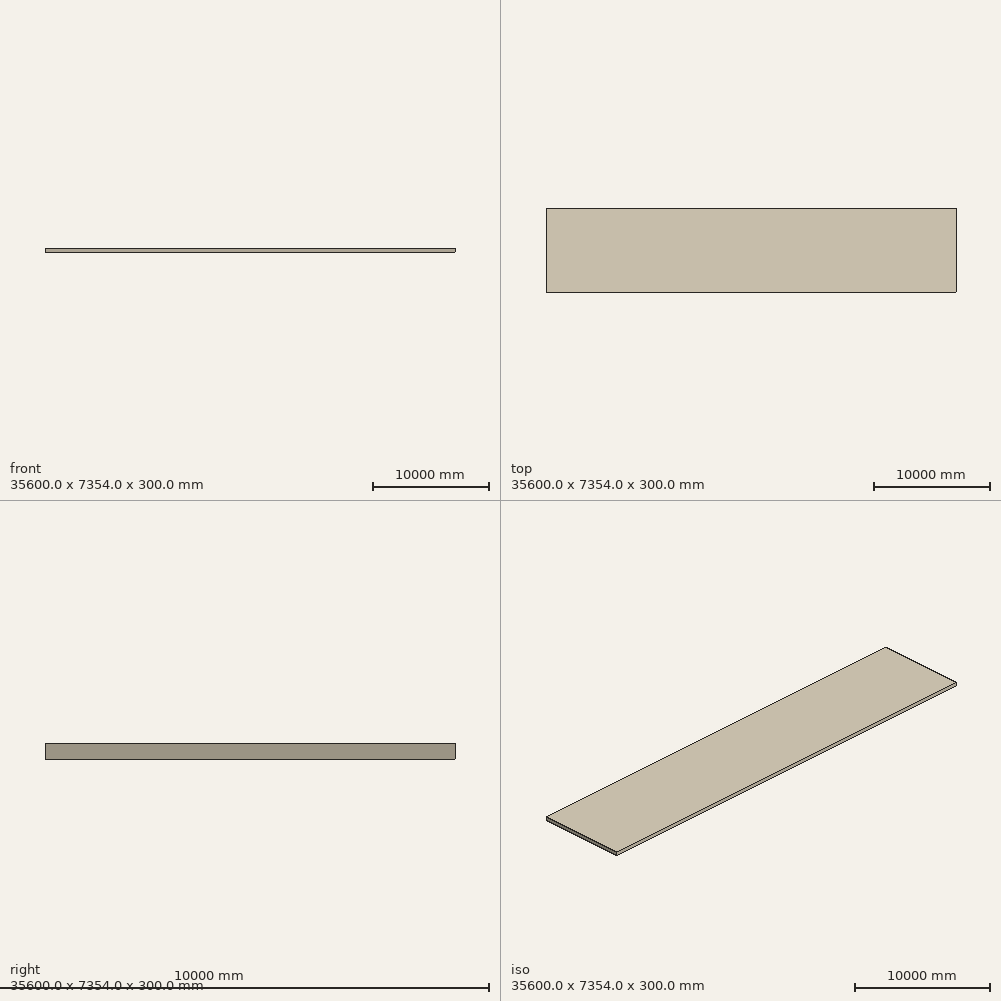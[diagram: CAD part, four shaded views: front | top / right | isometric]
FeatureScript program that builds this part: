
annotation { "Feature Type Name" : "Feature", "Feature Type Description" : "" }
export const myFeature = defineFeature(function(context is Context, id is Id, definition is map)
    precondition{}
    {
        {
            var Q0;
            Q0=qCreatedBy(makeId("Top.planeOp"),FACE);
            var sketch = newSketch(context, id + "F0", { "sketchPlane" : qUnion([Q0])});
            skLineSegment(sketch, "E0.bottom", {"start": v(17800, -3677) * mm, "end": v(-17800, -3677) * mm});
            skLineSegment(sketch, "E0.top", {"start": v(17800, 3677) * mm, "end": v(-17800, 3677) * mm});
            skLineSegment(sketch, "E0.left", {"start": v(17800, -3677) * mm, "end": v(17800, 3677) * mm});
            skLineSegment(sketch, "E0.right", {"start": v(-17800, -3677) * mm, "end": v(-17800, 3677) * mm});
            skPoint(sketch, "E0.middle", {"position": v(0, 0) * mm});
            skSolve(sketch);
        }
        {
            var Q0;
            Q0=qSketchRegion(id+"F0",true);
            extrude(context, id + "F1", {"entities" : qUnion([Q0]), "oppositeDirection" : true, "depth" : 300 * mm, "offsetDistance" : 25 * mm});
        }
    });
